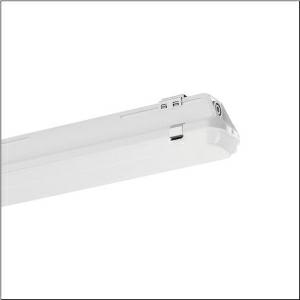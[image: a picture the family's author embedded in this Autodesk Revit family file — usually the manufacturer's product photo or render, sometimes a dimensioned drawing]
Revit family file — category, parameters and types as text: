
# Revit family: monsun_r__21_51fb107p430k005_710a
name_source: partatom
category: Lighting Fixtures
units: mm (PartAtom-declared; Revit-internal decimal feet)

## family parameters
Cut with Voids When Loaded = No
Host = Face
Light Source = No
Part Type = Normal
Room Calculation Point = No
Round Connector Dimension = Use Diameter
Shared = No

## types (1)
- Monsun® 21 (1 x LED, 3940 lm, 22.1 W, 4000K)
    Apparent Load = 22 VA
    CIE Flux Codes = 47 77 93 94 100
    Color Rendering = 80
    Color Temperature = 4000K
    Default Elevation = 1800 mm
    Description = Monsun® 21, damp-proof luminaire, chain hanger, primary optical cover: enclosure, of PMMA, light emission: direct distribution, primary light characteristic: symmetric, installation type: suspended mounting, surface-mounted, horizontal mounting, vertical mounting, LED, rated luminous flux: 3.940lm, luminous efficacy: 178lm/W, light colour: 840, colour temperature: 4000K, control gear: ON/OFF, with terminal, 3-pole, max. 2.5mm², through-wiring: 5x 2.5mm², mains connection: 220..240V, AC, 50/60Hz, rated input power: 22W, housing, of glass-fibre reinforced polyester, uncoated, bright grey, incl. chain hanger, length: 1.590mm, width: 90mm, height: 88mm, clip for enclosure, of stainless steel (V2A), ceiling mounting element, of stainless steel (V2A), chain hanger, of stainless steel (V2A), protection rating (complete): IP66, insulation class (complete): insulation class I (protective earthing), certification: CE, ENEC, VDE, UKCA, protection symbol: D, impact resistance: IK04, permissible operating ambient temperature: -25..+35°C, standard: EN 50419, EN 60598-2-1, corresponds to IFS (International Featured Standards) requirements for safety and quality in the food industry, for indoor or canopied outdoor use, no direct snow, no direct sun, no direct rain, LABS conformity tested according to VDMA 24364:2018-05, contact your sales advisor before using the luminaires in applications with unclear chemical exposure, large temperature fluctuations or condensation-forming humidity, packaging unit: 1 piece
    Height = 89 mm
    Lamp = 1 x LED
    Lamp Light Flux = 3940 lm
    Lamp Power = 22.1 W
    Lamp count = 1
    Length = 1590 mm
    Luminous efficacy = 178 lm/W
    Manufacturer = Siteco
    ModVariant = No
    Model = 51FB107P430K005
    Mounting Place = Ceiling
    Mounting Type = Surface mounted
    Number of Poles = 1
    OnlyDefault = Yes
    Power Factor = 1
    Product Name = Monsun® 21
    Product group = damp-proof luminaire
    ProductGroupID = 300
    Protection Class = Protection class I
    Protection Degree = IP 66
    RLX_Detail_Level = 1
    RLX_Emergency_Light_Flux = 0 lm
    RLX_Emergency_Type = 0
    RLX_Emergency_Type_DB = No
    RlxData = <blob elided: 88457 chars, md5=99fc1dbf>
    Socket = socket
    Standby Power = 0 W
    System Light Flux = 3940 lm
    System Power = 22 W
    Type Comments = Product without accessories
    Type Image = l_1319656.jpg
    URL = http://relux.com
    VarID = ---
    Voltage = 0 V
    Weight = 0.00 kg
    Width = 90 mm

## geometry (parser evidence)
native form markers: Blend x4, Sweep x12
no freeform markers — native parametric forms only
